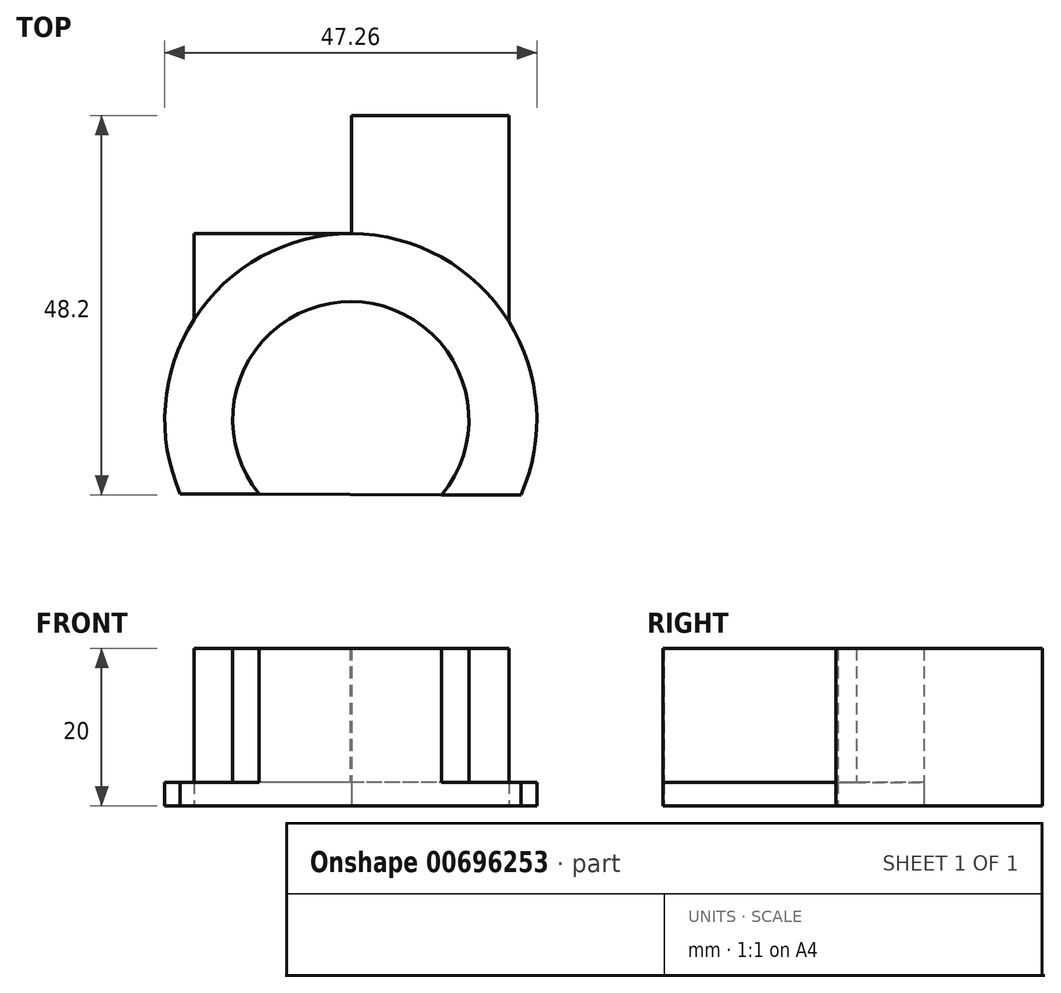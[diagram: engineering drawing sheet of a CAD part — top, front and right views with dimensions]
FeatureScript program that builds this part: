
annotation { "Feature Type Name" : "Feature", "Feature Type Description" : "" }
export const myFeature = defineFeature(function(context is Context, id is Id, definition is map)
    precondition{}
    {
        {
            var Q0;
            Q0=qCreatedBy(makeId("Top.planeOp"),FACE);
            var sketch = newSketch(context, id + "F0", { "sketchPlane" : qUnion([Q0])});
            skArc(sketch, "E0", {"start": v(-11.67, -9.43) * mm, "mid": v(0.1, 15) * mm, "end": v(11.55, -9.57) * mm});
            skLineSegment(sketch, "E1", {"start": v(-11.67, -9.43) * mm, "end": v(-21.67, -9.43) * mm});
            skLineSegment(sketch, "E2", {"start": v(11.55, -9.57) * mm, "end": v(21.55, -9.57) * mm});
            skArc(sketch, "E3", {"start": v(-21.67, -9.43) * mm, "mid": v(0.08, 23.63) * mm, "end": v(21.6, -9.57) * mm});
            skLineSegment(sketch, "E4", {"start": v(-11.67, -9.43) * mm, "end": v(11.55, -9.57) * mm});
            skLineSegment(sketch, "E5", {"start": v(-21.67, -9.43) * mm, "end": v(-11.67, -9.43) * mm});
            skLineSegment(sketch, "E6", {"start": v(11.55, -9.57) * mm, "end": v(21.6, -9.57) * mm});
            skLineSegment(sketch, "E7", {"start": v(-0.08, 23.63) * mm, "end": v(0, 38.63) * mm});
            skPoint(sketch, "E7.startSnap0", {"position": v(0.08, 23.63) * mm});
            skLineSegment(sketch, "E8.bottom", {"start": v(0.08, 23.63) * mm, "end": v(20.08, 23.63) * mm});
            skLineSegment(sketch, "E8.top", {"start": v(0.08, 38.63) * mm, "end": v(20.08, 38.63) * mm});
            skLineSegment(sketch, "E8.left", {"start": v(0.08, 23.63) * mm, "end": v(0.08, 38.63) * mm});
            skLineSegment(sketch, "E8.right", {"start": v(20.08, 23.63) * mm, "end": v(20.08, 38.63) * mm});
            skLineSegment(sketch, "E9.bottom", {"start": v(0.08, 23.63) * mm, "end": v(-19.92, 23.63) * mm});
            skLineSegment(sketch, "E9.top", {"start": v(0.08, 38.63) * mm, "end": v(-19.92, 38.63) * mm});
            skLineSegment(sketch, "E9.right", {"start": v(-19.92, 23.63) * mm, "end": v(-19.92, 38.63) * mm});
            skLineSegment(sketch, "E10", {"start": v(-19.92, 23.63) * mm, "end": v(-19.92, 12.7) * mm});
            skLineSegment(sketch, "E11", {"start": v(20.08, 23.63) * mm, "end": v(20.08, 12.46) * mm});
            skLineSegment(sketch, "E12.bottom", {"start": v(-19.92, 38.63) * mm, "end": v(20.08, 38.63) * mm});
            skLineSegment(sketch, "E12.top", {"start": v(-19.92, 23.63) * mm, "end": v(20.08, 23.63) * mm});
            skLineSegment(sketch, "E12.left", {"start": v(-19.92, 38.63) * mm, "end": v(-19.92, 23.63) * mm});
            skLineSegment(sketch, "E12.right", {"start": v(20.08, 38.63) * mm, "end": v(20.08, 23.63) * mm});
            skLineSegment(sketch, "E13", {"start": v(0.08, 38.63) * mm, "end": v(0.08, -9.5) * mm});
            skSolve(sketch);
        }
        {
            var Q0;
            Q0=makeQuery(id+"F0.imprint","IMPRINT",FACE,{"disambiguationData":[TD([[makeQuery(id+"F0.imprint","IMPRINT",EDGE,{"derivedFrom":sQuery(id+"F0.wireOp",EDGE,"E0")}),-1.0]])]});
            extrude(context, id + "F1", {"entities" : qUnion([Q0]), "depth" : 3 * mm, "offsetDistance" : 25 * mm});
        }
        {
            var Q0;
            {var subQ0=sQuery(id+"F0.wireOp",EDGE,"E0");Q0=makeQuery(id+"F0.imprint","IMPRINT",FACE,{"disambiguationData":[TD([[makeQuery(id+"F0.imprint","IMPRINT",EDGE,{"derivedFrom":subQ0}),1.0]])]});}
            var Q1;
            {var subQ0=sQuery(id+"F0.wireOp",EDGE,"E7");Q1=makeQuery(id+"F0.imprint","IMPRINT",FACE,{"disambiguationData":[TD([[makeQuery(id+"F0.imprint","IMPRINT",EDGE,{"derivedFrom":subQ0}),1.0]])]});}
            var Q2;
            Q2=makeQuery(id+"F0.imprint","IMPRINT",FACE,{"disambiguationData":[TD([[makeQuery(id+"F0.imprint","IMPRINT",EDGE,{"derivedFrom":sQuery(id+"F0.wireOp",EDGE,"E8.bottom")}),1.0]])]});
            var Q3;
            {var subQ0=sQuery(id+"F0.wireOp",EDGE,"E8.bottom");Q3=makeQuery(id+"F0.imprint","IMPRINT",FACE,{"disambiguationData":[TD([[makeQuery(id+"F0.imprint","IMPRINT",EDGE,{"derivedFrom":subQ0}),-1.0]])]});}
            var Q4;
            {var subQ3=sQuery(id+"F0.wireOp",EDGE,"E10");Q4=makeQuery(id+"F0.imprint","IMPRINT",FACE,{"disambiguationData":[TD([[makeQuery(id+"F0.imprint","IMPRINT",EDGE,{"derivedFrom":subQ3}),1.0]])]});}
            var Q5;
            {var subQ0=sQuery(id+"F0.wireOp",EDGE,"E8.left");Q5=makeQuery(id+"F0.imprint","IMPRINT",FACE,{"disambiguationData":[TD([[makeQuery(id+"F0.imprint","IMPRINT",EDGE,{"derivedFrom":subQ0}),-1.0]])]});}
            var Q6;
            {var subQ3=sQuery(id+"F0.wireOp",EDGE,"E11");Q6=makeQuery(id+"F0.imprint","IMPRINT",FACE,{"disambiguationData":[TD([[makeQuery(id+"F0.imprint","IMPRINT",EDGE,{"derivedFrom":subQ3}),-1.0]])]});}
            var Q7;
            {var subQ0=sQuery(id+"F0.wireOp",EDGE,"E12.right");Q7=makeQuery(id+"F0.imprint","IMPRINT",FACE,{"disambiguationData":[TD([[makeQuery(id+"F0.imprint","IMPRINT",EDGE,{"derivedFrom":subQ0}),-1.0]])]});}
            var Q8;
            {var subQ0=sQuery(id+"F0.wireOp",EDGE,"E5");Q8=makeQuery(id+"F0.imprint","IMPRINT",FACE,{"disambiguationData":[TD([[makeQuery(id+"F0.imprint","IMPRINT",EDGE,{"derivedFrom":subQ0}),1.0]])]});}
            extrude(context, id + "F2", {"entities" : qUnion([Q0, Q1, Q2, Q3, Q4, Q5, Q6, Q7, Q8]), "operationType" : NewBodyOperationType.ADD, "depth" : 20 * mm, "offsetDistance" : 25 * mm});
        }
    });
